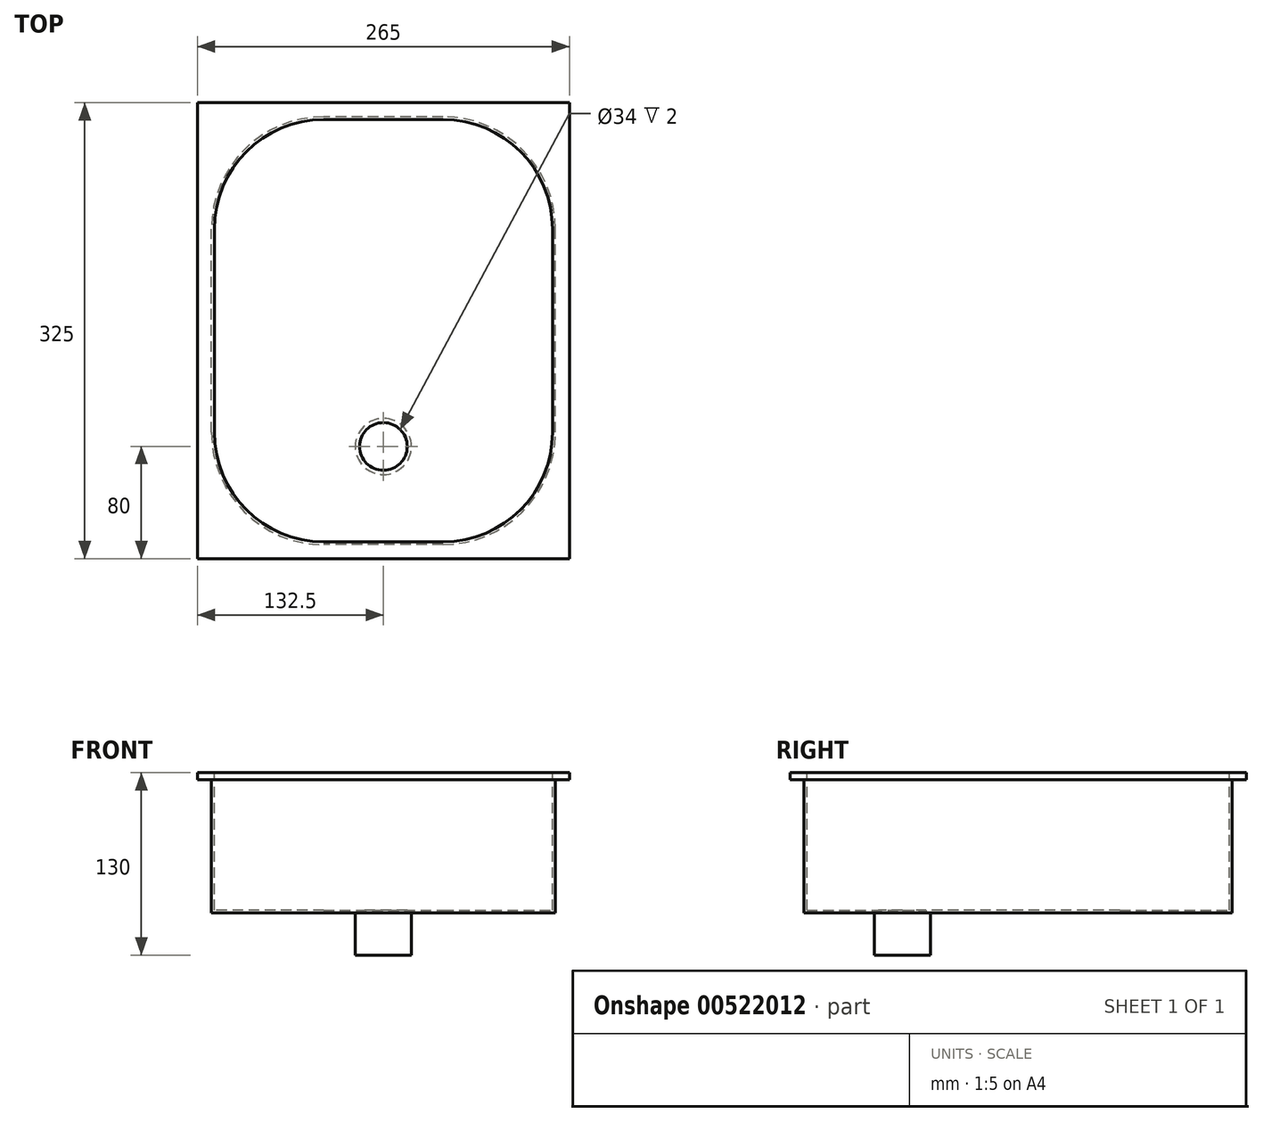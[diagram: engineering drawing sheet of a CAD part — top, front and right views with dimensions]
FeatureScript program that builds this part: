
annotation { "Feature Type Name" : "Feature", "Feature Type Description" : "" }
export const myFeature = defineFeature(function(context is Context, id is Id, definition is map)
    precondition{}
    {
        {
            var Q0;
            Q0=qCreatedBy(makeId("Top.planeOp"),FACE);
            var sketch = newSketch(context, id + "F0", { "sketchPlane" : qUnion([Q0])});
            skLineSegment(sketch, "E0.bottom", {"start": v(0, 0) * mm, "end": v(265, 0) * mm});
            skLineSegment(sketch, "E0.top", {"start": v(0, 325) * mm, "end": v(265, 325) * mm});
            skLineSegment(sketch, "E0.left", {"start": v(0, 0) * mm, "end": v(0, 325) * mm});
            skLineSegment(sketch, "E0.right", {"start": v(265, 0) * mm, "end": v(265, 325) * mm});
            skSolve(sketch);
        }
        {
            var Q0;
            Q0=makeQuery(id+"F0.imprint","IMPRINT",FACE,{"disambiguationData":[TD([[makeQuery(id+"F0.imprint","IMPRINT",EDGE,{"derivedFrom":sQuery(id+"F0.wireOp",EDGE,"E0.bottom")}),1.0]])]});
            extrude(context, id + "F1", {"entities" : qUnion([Q0]), "depth" : 5 * mm, "offsetDistance" : 25 * mm});
        }
        {
            var Q0;
            Q0=makeQuery(id+"F1.opExtrude","CAP_FACE",FACE,{"disambiguationData":[OSD([sQuery(id+"F0.wireOp",EDGE,"E0.bottom"),sQuery(id+"F0.wireOp",EDGE,"E0.top"),sQuery(id+"F0.wireOp",EDGE,"E0.left"),sQuery(id+"F0.wireOp",EDGE,"E0.right")])],"isStart":true});
            var sketch = newSketch(context, id + "F2", { "sketchPlane" : qUnion([Q0])});
            skLineSegment(sketch, "E1.bottom", {"start": v(175, -10) * mm, "end": v(90, -10) * mm});
            skLineSegment(sketch, "E1.top", {"start": v(175, -315) * mm, "end": v(90, -315) * mm});
            skLineSegment(sketch, "E1.left", {"start": v(255, -90) * mm, "end": v(255, -235) * mm});
            skLineSegment(sketch, "E1.right", {"start": v(10, -90) * mm, "end": v(10, -235) * mm});
            skPoint(sketch, "E2.visualSharp", {"position": v(255, -10) * mm});
            skArc(sketch, "E2.filletArc", {"start": v(255, -90) * mm, "mid": v(231.57, -33.43) * mm, "end": v(175, -10) * mm});
            skPoint(sketch, "E3.visualSharp", {"position": v(10, -10) * mm});
            skArc(sketch, "E3.filletArc", {"start": v(90, -10) * mm, "mid": v(33.43, -33.43) * mm, "end": v(10, -90) * mm});
            skPoint(sketch, "E4.visualSharp", {"position": v(10, -315) * mm});
            skArc(sketch, "E4.filletArc", {"start": v(10, -235) * mm, "mid": v(33.43, -291.57) * mm, "end": v(90, -315) * mm});
            skPoint(sketch, "E5.visualSharp", {"position": v(255, -315) * mm});
            skArc(sketch, "E5.filletArc", {"start": v(175, -315) * mm, "mid": v(231.57, -291.57) * mm, "end": v(255, -235) * mm});
            skArc(sketch, "E6.0", {"start": v(253, -90) * mm, "mid": v(230.15, -34.85) * mm, "end": v(175, -12) * mm});
            skLineSegment(sketch, "E6.1", {"start": v(175, -12) * mm, "end": v(90, -12) * mm});
            skLineSegment(sketch, "E6.2", {"start": v(253, -90) * mm, "end": v(253, -235) * mm});
            skArc(sketch, "E6.3", {"start": v(90, -12) * mm, "mid": v(34.85, -34.85) * mm, "end": v(12, -90) * mm});
            skArc(sketch, "E6.4", {"start": v(175, -313) * mm, "mid": v(230.15, -290.15) * mm, "end": v(253, -235) * mm});
            skLineSegment(sketch, "E6.5", {"start": v(175, -313) * mm, "end": v(90, -313) * mm});
            skArc(sketch, "E6.6", {"start": v(12, -235) * mm, "mid": v(34.85, -290.15) * mm, "end": v(90, -313) * mm});
            skLineSegment(sketch, "E6.7", {"start": v(12, -90) * mm, "end": v(12, -235) * mm});
            skSolve(sketch);
        }
        {
            var Q0;
            Q0=makeQuery(id+"F2.imprint","IMPRINT",FACE,{"disambiguationData":[TD([[makeQuery(id+"F2.imprint","IMPRINT",EDGE,{"derivedFrom":sQuery(id+"F2.wireOp",EDGE,"E1.bottom")}),1.0]])]});
            var Q1;
            Q1=makeQuery(id+"F2.imprint","IMPRINT",FACE,{"disambiguationData":[TD([[makeQuery(id+"F2.imprint","IMPRINT",EDGE,{"derivedFrom":sQuery(id+"F2.wireOp",EDGE,"E6.0")}),1.0]])]});
            extrude(context, id + "F3", {"entities" : qUnion([Q0, Q1]), "operationType" : NewBodyOperationType.ADD, "depth" : 95 * mm, "offsetDistance" : 25 * mm});
        }
        {
            var Q0;
            Q0 = qSketchRegion(id + "F2", true);
            extrude(context, id + "F4", {"entities" : qUnion([Q0]), "operationType" : NewBodyOperationType.REMOVE, "oppositeDirection" : true, "depth" : 25 * mm, "offsetDistance" : 25 * mm});
        }
        {
            var Q0;
            Q0=makeQuery(id+"F4.boolean.opBoolean","SPLIT",FACE,{"disambiguationData":[TD([makeQuery(id+"F4.opExtrude","SWEPT_FACE",FACE,{"disambiguationData":[OSD([sQuery(id+"F2.wireOp",EDGE,"E6.0")])]})])],"derivedFrom":makeQuery(id+"F1.opExtrude","CAP_FACE",FACE,{"disambiguationData":[OSD([sQuery(id+"F0.wireOp",EDGE,"E0.bottom"),sQuery(id+"F0.wireOp",EDGE,"E0.top"),sQuery(id+"F0.wireOp",EDGE,"E0.left"),sQuery(id+"F0.wireOp",EDGE,"E0.right")])],"isStart":false})});
            extrude(context, id + "F5", {"entities" : qUnion([Q0]), "operationType" : NewBodyOperationType.REMOVE, "oppositeDirection" : true, "depth" : 98 * mm, "offsetDistance" : 25 * mm});
        }
        {
            var Q0;
            Q0=makeQuery(id+"F3.opExtrude","CAP_FACE",FACE,{"disambiguationData":[OSD([sQuery(id+"F2.wireOp",EDGE,"E1.bottom"),sQuery(id+"F2.wireOp",EDGE,"E1.top"),sQuery(id+"F2.wireOp",EDGE,"E1.left"),sQuery(id+"F2.wireOp",EDGE,"E1.right"),sQuery(id+"F2.wireOp",EDGE,"E2.filletArc"),sQuery(id+"F2.wireOp",EDGE,"E3.filletArc"),sQuery(id+"F2.wireOp",EDGE,"E4.filletArc"),sQuery(id+"F2.wireOp",EDGE,"E5.filletArc")])],"isStart":false});
            var sketch = newSketch(context, id + "F6", { "sketchPlane" : qUnion([Q0])});
            skCircle(sketch, "E7", {"center": v(132.5, -80) * mm, "radius": 20 * mm});
            skCircle(sketch, "E8", {"center": v(132.5, -80) * mm, "radius": 17 * mm});
            skLineSegment(sketch, "E9", {"start": v(132.5, -10) * mm, "end": v(132.5, -315) * mm, "construction": true});
            skSolve(sketch);
        }
        {
            var Q0;
            Q0=makeQuery(id+"F6.imprint","IMPRINT",FACE,{"disambiguationData":[TD([[makeQuery(id+"F6.imprint","IMPRINT",EDGE,{"derivedFrom":sQuery(id+"F6.wireOp",EDGE,"E8")}),1.0]])]});
            extrude(context, id + "F7", {"entities" : qUnion([Q0]), "operationType" : NewBodyOperationType.REMOVE, "oppositeDirection" : true, "depth" : 25 * mm, "offsetDistance" : 25 * mm});
        }
        {
            var Q0;
            Q0=makeQuery(id+"F6.imprint","IMPRINT",FACE,{"disambiguationData":[TD([[makeQuery(id+"F6.imprint","IMPRINT",EDGE,{"derivedFrom":sQuery(id+"F6.wireOp",EDGE,"E7")}),1.0]])]});
            var Q1;
            Q1=makeQuery(id+"F6.imprint","IMPRINT",FACE,{"disambiguationData":[TD([[makeQuery(id+"F6.imprint","IMPRINT",EDGE,{"derivedFrom":sQuery(id+"F6.wireOp",EDGE,"E8")}),1.0]])]});
            extrude(context, id + "F8", {"entities" : qUnion([Q0, Q1]), "operationType" : NewBodyOperationType.ADD, "depth" : 30 * mm, "offsetDistance" : 25 * mm});
        }
        {
            var Q0;
            Q0=makeQuery(id+"F4.boolean.opBoolean","COPY",FACE,{"derivedFrom":makeQuery(id+"F4.opExtrude","CAP_FACE",FACE,{"disambiguationData":[OSD([sQuery(id+"F2.wireOp",EDGE,"E1.bottom"),sQuery(id+"F2.wireOp",EDGE,"E1.top"),sQuery(id+"F2.wireOp",EDGE,"E1.left"),sQuery(id+"F2.wireOp",EDGE,"E1.right"),sQuery(id+"F2.wireOp",EDGE,"E2.filletArc"),sQuery(id+"F2.wireOp",EDGE,"E3.filletArc"),sQuery(id+"F2.wireOp",EDGE,"E4.filletArc"),sQuery(id+"F2.wireOp",EDGE,"E5.filletArc"),sQuery(id+"F2.wireOp",EDGE,"E6.0"),sQuery(id+"F2.wireOp",EDGE,"E6.1"),sQuery(id+"F2.wireOp",EDGE,"E6.2"),sQuery(id+"F2.wireOp",EDGE,"E6.3"),sQuery(id+"F2.wireOp",EDGE,"E6.4"),sQuery(id+"F2.wireOp",EDGE,"E6.5"),sQuery(id+"F2.wireOp",EDGE,"E6.6"),sQuery(id+"F2.wireOp",EDGE,"E6.7")])],"isStart":true})});
            extrude(context, id + "F9", {"entities" : qUnion([Q0]), "operationType" : NewBodyOperationType.ADD, "depth" : 5 * mm, "offsetDistance" : 25 * mm});
        }
    });
